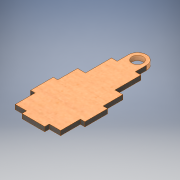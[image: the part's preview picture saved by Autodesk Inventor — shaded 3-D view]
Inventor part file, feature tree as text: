
AUTODESK INVENTOR PART (.ipt)
format: ipt  version: 2019 (Build 230136000, 136)  size: 149,504 bytes
history: native  units: mm
features: other x1, extrude x1, sketch x1
ambient origin geometry x8: Origin, YZ Plane, XZ Plane, XY Plane, X Axis, Y Axis, Z Axis, Center Point
bodies: Body1 (feature_tree)
feature tree (3):
  other  "Твердое тело1"
  extrude  "Выдавливание1"  Depth=16.0mm
  sketch  "Эскиз1"
